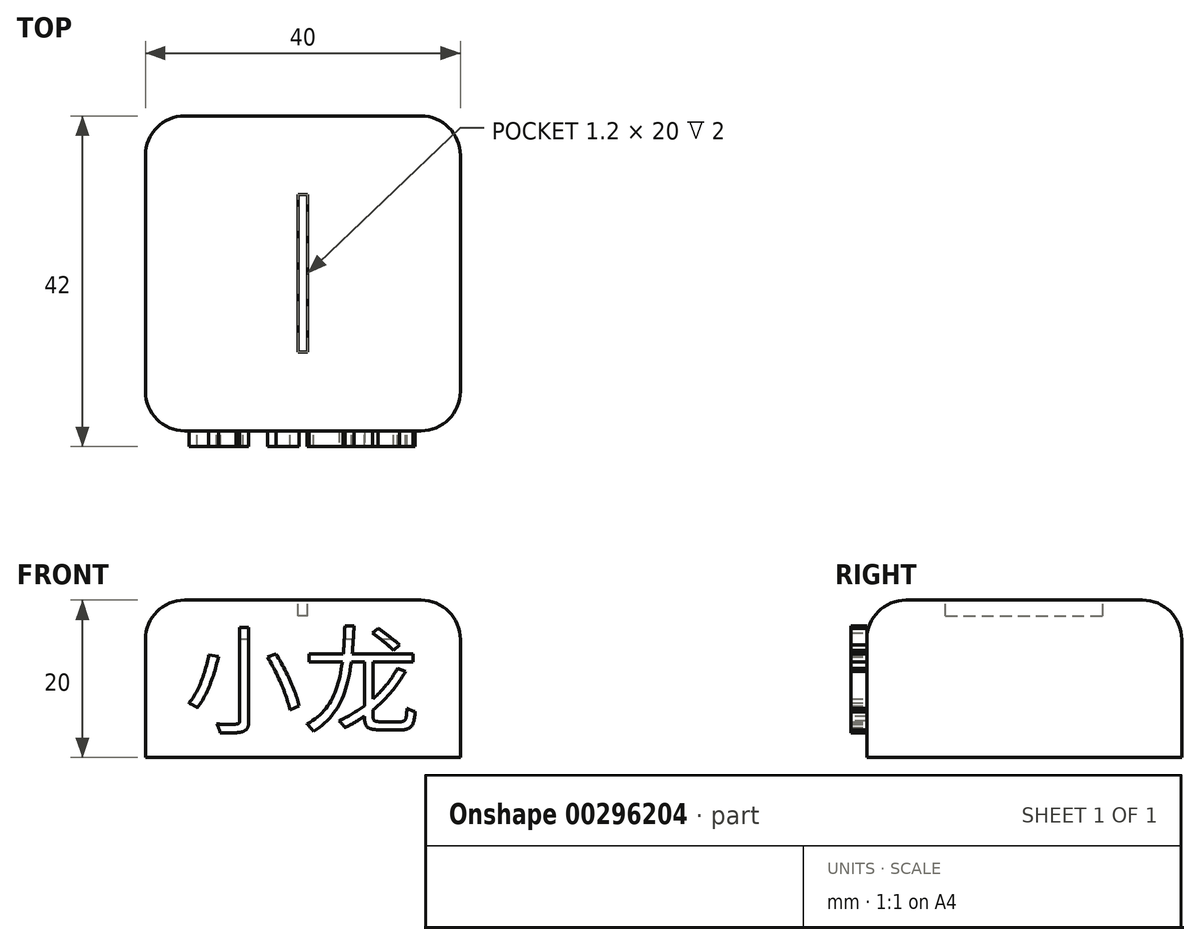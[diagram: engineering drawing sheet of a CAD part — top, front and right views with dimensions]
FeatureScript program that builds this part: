
annotation { "Feature Type Name" : "Feature", "Feature Type Description" : "" }
export const myFeature = defineFeature(function(context is Context, id is Id, definition is map)
    precondition{}
    {
        {
            var Q0;
            Q0=qCreatedBy(makeId("Top.planeOp"),FACE);
            var sketch = newSketch(context, id + "F0", { "sketchPlane" : qUnion([Q0])});
            skLineSegment(sketch, "E0.bottom", {"start": v(20, -20) * mm, "end": v(-20, -20) * mm});
            skLineSegment(sketch, "E0.top", {"start": v(20, 20) * mm, "end": v(-20, 20) * mm});
            skLineSegment(sketch, "E0.left", {"start": v(20, -20) * mm, "end": v(20, 20) * mm});
            skLineSegment(sketch, "E0.right", {"start": v(-20, -20) * mm, "end": v(-20, 20) * mm});
            skPoint(sketch, "E0.middle", {"position": v(0, 0) * mm});
            skLineSegment(sketch, "E1.bottom", {"start": v(0.6, -10) * mm, "end": v(-0.6, -10) * mm});
            skLineSegment(sketch, "E1.top", {"start": v(0.6, 10) * mm, "end": v(-0.6, 10) * mm});
            skLineSegment(sketch, "E1.left", {"start": v(0.6, -10) * mm, "end": v(0.6, 10) * mm});
            skLineSegment(sketch, "E1.right", {"start": v(-0.6, -10) * mm, "end": v(-0.6, 10) * mm});
            skSolve(sketch);
        }
        {
            var Q0;
            Q0=makeQuery(id+"F0.imprint","IMPRINT",FACE,{"disambiguationData":[TD([[makeQuery(id+"F0.imprint","IMPRINT",EDGE,{"derivedFrom":sQuery(id+"F0.wireOp",EDGE,"E0.bottom")}),-1.0]])]});
            var Q1;
            Q1=makeQuery(id+"F0.imprint","IMPRINT",FACE,{"disambiguationData":[TD([[makeQuery(id+"F0.imprint","IMPRINT",EDGE,{"derivedFrom":sQuery(id+"F0.wireOp",EDGE,"E1.bottom")}),-1.0]])]});
            extrude(context, id + "F1", {"entities" : qUnion([Q0, Q1]), "oppositeDirection" : true, "depth" : 20 * mm});
        }
        {
            var Q0;
            Q0=makeQuery(id+"F0.imprint","IMPRINT",FACE,{"disambiguationData":[TD([[makeQuery(id+"F0.imprint","IMPRINT",EDGE,{"derivedFrom":sQuery(id+"F0.wireOp",EDGE,"E1.bottom")}),-1.0]])]});
            extrude(context, id + "F2", {"entities" : qUnion([Q0]), "operationType" : NewBodyOperationType.REMOVE, "oppositeDirection" : true, "depth" : 2 * mm});
        }
        {
            var Q0;
            Q0=makeQuery(id+"F2.boolean.opBoolean","COPY",EDGE,{"derivedFrom":makeQuery(id+"F2.opExtrude","CAP_EDGE",EDGE,{"disambiguationData":[OSD([sQuery(id+"F0.wireOp",EDGE,"E1.left")])],"isStart":true})});
            var Q1;
            Q1=makeQuery(id+"F2.boolean.opBoolean","COPY",EDGE,{"derivedFrom":makeQuery(id+"F2.opExtrude","CAP_EDGE",EDGE,{"disambiguationData":[OSD([sQuery(id+"F0.wireOp",EDGE,"E1.right")])],"isStart":true})});
            var Q2;
            Q2=makeQuery(id+"F1.opExtrude","SWEPT_EDGE",EDGE,{"disambiguationData":[OSD([sQuery(id+"F0.wireOp",EDGE,"E0.bottom"),sQuery(id+"F0.wireOp",EDGE,"E0.left")])]});
            var Q3;
            Q3=makeQuery(id+"F1.opExtrude","SWEPT_EDGE",EDGE,{"disambiguationData":[OSD([sQuery(id+"F0.wireOp",EDGE,"E0.top"),sQuery(id+"F0.wireOp",EDGE,"E0.left")])]});
            var Q4;
            Q4=makeQuery(id+"F1.opExtrude","CAP_EDGE",EDGE,{"disambiguationData":[OSD([sQuery(id+"F0.wireOp",EDGE,"E0.left")])],"isStart":true});
            var Q5;
            Q5=makeQuery(id+"F1.opExtrude","SWEPT_EDGE",EDGE,{"disambiguationData":[OSD([sQuery(id+"F0.wireOp",EDGE,"E0.bottom"),sQuery(id+"F0.wireOp",EDGE,"E0.right")])]});
            var Q6;
            Q6=makeQuery(id+"F1.opExtrude","SWEPT_EDGE",EDGE,{"disambiguationData":[OSD([sQuery(id+"F0.wireOp",EDGE,"E0.top"),sQuery(id+"F0.wireOp",EDGE,"E0.right")])]});
            var Q7;
            Q7=makeQuery(id+"F1.opExtrude","CAP_EDGE",EDGE,{"disambiguationData":[OSD([sQuery(id+"F0.wireOp",EDGE,"E0.top")])],"isStart":true});
            var Q8;
            Q8=makeQuery(id+"F1.opExtrude","CAP_EDGE",EDGE,{"disambiguationData":[OSD([sQuery(id+"F0.wireOp",EDGE,"E0.right")])],"isStart":true});
            var Q9;
            Q9=makeQuery(id+"F1.opExtrude","CAP_EDGE",EDGE,{"disambiguationData":[OSD([sQuery(id+"F0.wireOp",EDGE,"E0.bottom")])],"isStart":true});
            fillet(context, id + "F3", {"entities" : qUnion([Q0, Q1, Q2, Q3, Q4, Q5, Q6, Q7, Q8, Q9]), "radius" : 5 * mm, "tangentPropagation" : true, "allowEdgeOverflow" : false});
        }
        {
            var Q0;
            Q0=makeQuery(id+"F1.opExtrude","SWEPT_FACE",FACE,{"disambiguationData":[OSD([sQuery(id+"F0.wireOp",EDGE,"E0.bottom")])]});
            var sketch = newSketch(context, id + "F4", { "sketchPlane" : qUnion([Q0])});
            skText(sketch, "E2", { "text": "小龙", "fontName": "NotoSansCJKsc-Regular.otf"});
            const initialGuessF4  = {"E2": [-0.015, -0.01576, 1, 0, 0.01076]};
            skSetInitialGuess(sketch, initialGuessF4);
            skSolve(sketch);
        }
        {
            var Q0;
            {var subQ0=sQuery(id+"F4.wireOp",EDGE,"E2.sketch_text.stroke-19");Q0=makeQuery(id+"F4.imprint","IMPRINT",FACE,{"disambiguationData":[TD([[makeQuery(id+"F4.imprint","IMPRINT",EDGE,{"derivedFrom":subQ0}),1.0]])]});}
            var Q1;
            {var subQ0=sQuery(id+"F4.wireOp",EDGE,"E2.sketch_text.stroke-17");Q1=makeQuery(id+"F4.imprint","IMPRINT",FACE,{"disambiguationData":[TD([[makeQuery(id+"F4.imprint","IMPRINT",EDGE,{"derivedFrom":subQ0}),1.0]])]});}
            var Q2;
            Q2=makeQuery(id+"F4.imprint","IMPRINT",FACE,{"disambiguationData":[TD([[makeQuery(id+"F4.imprint","IMPRINT",EDGE,{"derivedFrom":sQuery(id+"F4.wireOp",EDGE,"E2.sketch_text.stroke-20")}),1.0]])]});
            var Q3;
            {var subQ0=sQuery(id+"F4.wireOp",EDGE,"E2.sketch_text.stroke-30");Q3=makeQuery(id+"F4.imprint","IMPRINT",FACE,{"disambiguationData":[TD([[makeQuery(id+"F4.imprint","IMPRINT",EDGE,{"derivedFrom":subQ0}),1.0]])]});}
            var Q4;
            Q4=makeQuery(id+"F4.imprint","IMPRINT",FACE,{"disambiguationData":[TD([[makeQuery(id+"F4.imprint","IMPRINT",EDGE,{"derivedFrom":sQuery(id+"F4.wireOp",EDGE,"E2.sketch_text.stroke-8")}),1.0]])]});
            var Q5;
            Q5=makeQuery(id+"F4.imprint","IMPRINT",FACE,{"disambiguationData":[TD([[makeQuery(id+"F4.imprint","IMPRINT",EDGE,{"derivedFrom":sQuery(id+"F4.wireOp",EDGE,"E2.sketch_text.stroke-12")}),1.0]])]});
            var Q6;
            {var subQ0=sQuery(id+"F4.wireOp",EDGE,"E2.sketch_text.stroke-1");Q6=makeQuery(id+"F4.imprint","IMPRINT",FACE,{"disambiguationData":[TD([[makeQuery(id+"F4.imprint","IMPRINT",EDGE,{"derivedFrom":subQ0}),1.0]])]});}
            var Q7;
            {var subQ0=sQuery(id+"F4.wireOp",EDGE,"E2.sketch_text.stroke-7");Q7=makeQuery(id+"F4.imprint","IMPRINT",FACE,{"disambiguationData":[TD([[makeQuery(id+"F4.imprint","IMPRINT",EDGE,{"derivedFrom":subQ0}),1.0]])]});}
            extrude(context, id + "F5", {"entities" : qUnion([Q0, Q1, Q2, Q3, Q4, Q5, Q6, Q7]), "operationType" : NewBodyOperationType.ADD, "depth" : 2 * mm});
        }
    });
